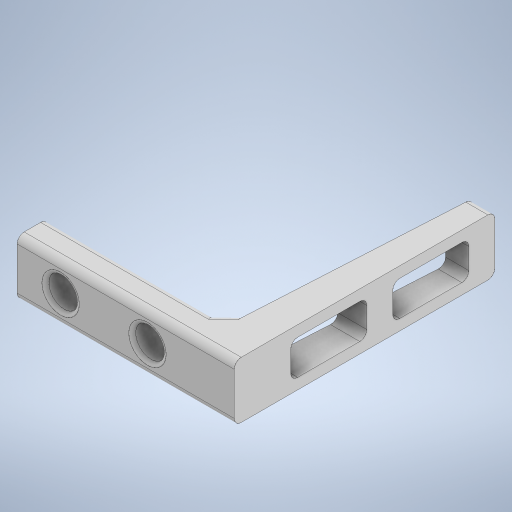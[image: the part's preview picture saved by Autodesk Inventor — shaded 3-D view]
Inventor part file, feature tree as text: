
AUTODESK INVENTOR PART (.ipt)
format: ipt  version: 2024.2 (Build 282272000, 272)  size: 324,608 bytes
history: native  units: mm
features: extrude x3, sketch x3, fillet x2, projected_geometry x2, other x1, chamfer x1
ambient origin geometry x8: Origin, YZ Plane, XZ Plane, XY Plane, X Axis, Y Axis, Z Axis, Center Point
bodies: Body1 (feature_tree)
feature tree (12):
  other  "Bryła1"
  extrude  "Wyciągnięcie proste1"  Depth=25.0mm
  extrude  "Wyciągnięcie proste2"  Depth=30.0mm
  extrude  "Wyciągnięcie proste3"  Depth=3.5mm
  chamfer  "Faza1"  Distance=2.5mm
  fillet  "Zaokrąglenie1"  Radius=4.0mm
  fillet  "Zaokrąglenie2"  Radius=6.5mm
  sketch  "Szkic1"
  sketch  "Szkic2"
  projected_geometry  "Pętla rzutowana1"
  sketch  "Szkic3"
  projected_geometry  "Pętla rzutowana2"
